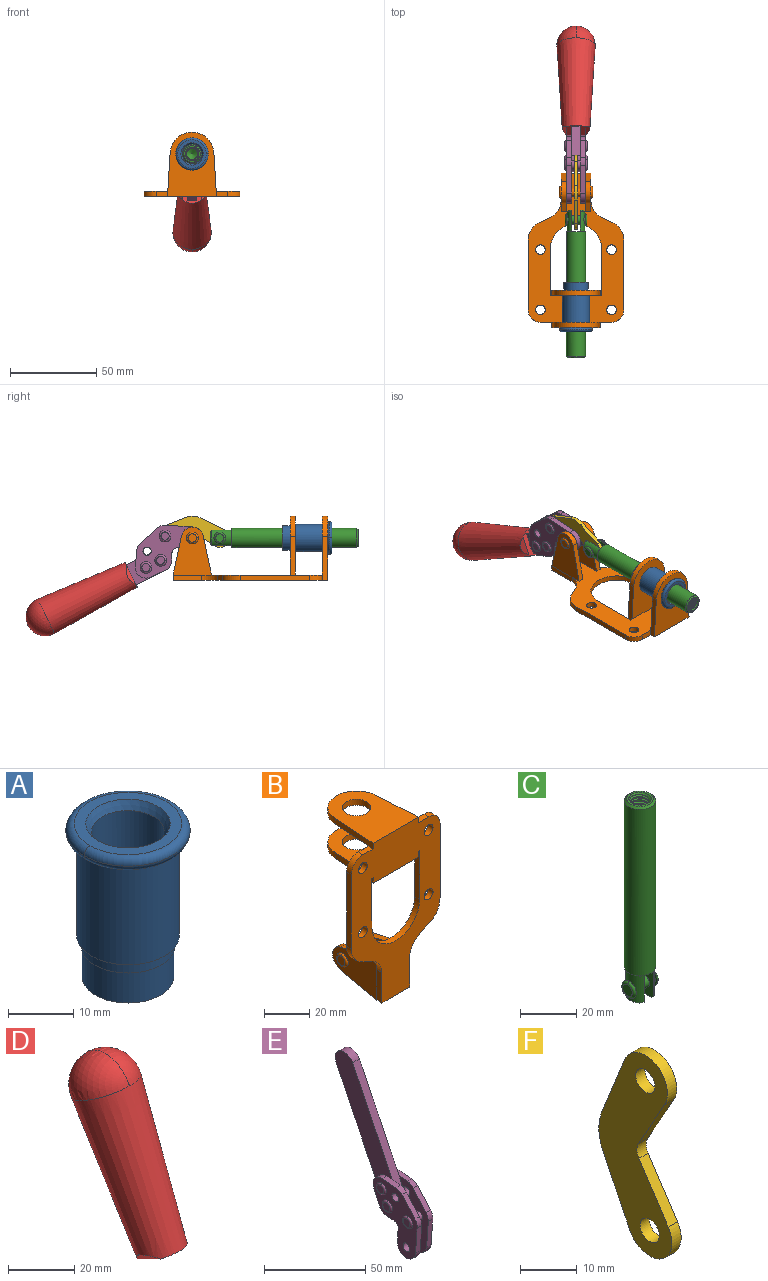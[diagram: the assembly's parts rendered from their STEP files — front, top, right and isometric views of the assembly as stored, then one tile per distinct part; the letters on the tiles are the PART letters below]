
ASSEMBLY  parts=6 mates=6
PART A: 15 faces, bbox 20.6x20.6x28.7 mm
  f0: torus R=8.26mm, axis (0,0,1), area 56.8mm2, adj f1,f10,f12
  f1: torus R=8.26mm, axis (0,0,1), area 56.8mm2, adj f0,f6,f13
  f2: cylinder r=5.59mm len=25.91mm, axis (0,0,1), area 909.6mm2, adj f3,f4
  f3: cone r=6.86mm half-angle=45deg, axis (0,0,-1), area 70.2mm2, adj f2,f14
  f4: cone r=6.47mm half-angle=30deg, axis (0,0,1), area 66.7mm2, adj f2,f13
  f5: cylinder r=7.04mm len=14.07mm, axis (0,0,1), area 252.6mm2, adj f11,f14
  f6: torus R=8.26mm, axis (0,0,1), area 56.8mm2, adj f1,f12,f13
  f7: cylinder r=7.16mm len=14.33mm, axis (0,0,1), area 91.5mm2, adj f9,f11
  f8: cylinder r=7.86mm len=18.42mm, axis (0,0,1), area 909.6mm2, adj f9,f10
  f9: plane 15.72x15.72mm, normal (0,0,-1), area 33mm2, adj f7,f8
  f10: plane 16.51x16.51mm, normal (0,0,-1), area 19.9mm2, adj f0,f8,f12
  f11: plane 14.33x14.33mm, normal (0,0,-1), area 5.7mm2, adj f5,f7
  f12: torus R=8.26mm, axis (0,0,1), area 56.8mm2, adj f0,f6,f10
  f13: plane 16.51x16.51mm, normal (0,0,1), area 82.7mm2, adj f1,f4,f6
  f14: plane 14.07x14.07mm, normal (0,0,-1), area 7.8mm2, adj f3,f5
PART B: 55 faces, bbox 55.7x37.4x89.8 mm
  f0: torus R=2.41mm, axis (-1,0,0), area 15mm2, adj f11,f15,f25
  f1: torus R=2.41mm, axis (-1,0,0), area 15mm2, adj f10,f12,f22
  f2: cylinder r=2.78mm len=5.56mm, axis (0,-1,0), area 54.2mm2, adj f30,f54
  f3: cylinder r=14.99mm len=29.97mm, axis (0,-1,0), area 145.9mm2, adj f30,f49,f53,f54
  f4: cylinder r=2.78mm len=5.56mm, axis (0,-1,0), area 54.2mm2, adj f30,f54
  f5: cylinder r=2.78mm len=5.56mm, axis (0,-1,0), area 54.2mm2, adj f30,f54
  f6: cylinder r=2.78mm len=5.56mm, axis (0,-1,0), area 54.2mm2, adj f30,f54
  f7: cylinder r=6.35mm len=12.7mm, axis (0,0,1), area 123.6mm2, adj f27,f51
  f8: cylinder r=6.35mm len=12.7mm, axis (0,0,-1), area 124.7mm2, adj f21,f35
  f9: cylinder r=2.41mm len=11.18mm, axis (-1,0,0), area 169.4mm2, adj f16,f19
  f10: plane 4.83x4.83mm, normal (1,0,0), area 18.3mm2, adj f1,f12
  f11: plane 4.83x4.83mm, normal (-1,0,0), area 18.3mm2, adj f0,f15
  f12: torus R=2.41mm, axis (-1,0,0), area 15mm2, adj f1,f10,f22
  f13: cylinder r=6.35mm len=12.41mm, axis (1,0,0), area 53.4mm2, adj f18,f19,f22,f23
  f14: cylinder r=6.35mm len=12.41mm, axis (-1,0,0), area 53.4mm2, adj f16,f17,f24,f25
  f15: torus R=2.41mm, axis (-1,0,0), area 15mm2, adj f0,f11,f25
  f16: plane 27.86x22.35mm, normal (1,0,0), area 425.4mm2, adj f9,f14,f17,f24,f30
  f17: plane 22.86x4.97mm, normal (0,0.21,0.98), area 72.5mm2, adj f14,f16,f25,f30
  f18: plane 22.86x4.97mm, normal (0,0.21,0.98), area 72.5mm2, adj f13,f19,f22,f30
  f19: plane 27.86x22.35mm, normal (-1,0,0), area 425.4mm2, adj f9,f13,f18,f23,f30
  f20: cylinder r=12.7mm len=25.35mm, axis (0,0,-1), area 119.8mm2, adj f21,f34,f35,f36
  f21: plane 34.21x28.07mm, normal (0,0,-1), area 702.4mm2, adj f8,f20,f30,f34,f36
  f22: plane 27.96x22.45mm, normal (1,0,0), area 407.2mm2, adj f1,f12,f13,f18,f23,f30,f42,f43
  f23: plane 22.86x4.97mm, normal (0,0.21,-0.98), area 72.5mm2, adj f13,f19,f22,f44
  f24: plane 22.86x4.97mm, normal (0,0.21,-0.98), area 72.5mm2, adj f14,f16,f25,f44
  f25: plane 27.86x22.35mm, normal (-1,0,0), area 407.1mm2, adj f0,f14,f15,f17,f24,f30,f45,f46
  f26: plane 3.1x0.95mm, normal (0,0,-1), area 2.7mm2, adj f30,f49,f50,f54
  f27: plane 34.21x28.07mm, normal (0,0,1), area 702.4mm2, adj f7,f28,f30,f50,f52
  f28: cylinder r=12.7mm len=25.35mm, axis (0,0,1), area 118.8mm2, adj f27,f50,f51,f52
  f29: plane 3.1x0.95mm, normal (0,0,-1), area 2.7mm2, adj f30,f52,f53,f54
  f30: plane 86.54x55.63mm, normal (0,1,0), area 2362.9mm2, adj f2,f3,f4,f5,f6,f16,f17,f18
  f31: plane 40.56x3.1mm, normal (-1,0,0), area 125.7mm2, adj f30,f32,f48,f54
  f32: cylinder r=7.11mm len=7.11mm, axis (0,-1,0), area 34.6mm2, adj f30,f31,f33,f54
  f33: plane 6.67x3.1mm, normal (0,0,1), area 20.4mm2, adj f30,f32,f34,f54
  f34: plane 25.39x3.13mm, normal (-1,0.06,0), area 79.5mm2, adj f20,f21,f33,f35,f54
  f35: plane 37.31x28.45mm, normal (0,0,1), area 789.9mm2, adj f8,f20,f34,f36,f54
  f36: plane 25.39x3.13mm, normal (1,0.06,0), area 79.5mm2, adj f20,f21,f35,f37,f54
  f37: plane 6.67x3.1mm, normal (0,0,1), area 20.4mm2, adj f30,f36,f38,f54
  f38: cylinder r=7.11mm len=7.11mm, axis (0,-1,0), area 34.6mm2, adj f30,f37,f39,f54
  f39: plane 40.56x3.1mm, normal (1,0,0), area 125.7mm2, adj f30,f38,f40,f54
  f40: cylinder r=11.18mm len=10.16mm, axis (0,-1,0), area 39.5mm2, adj f30,f39,f41,f54
  f41: plane 6.09x3.1mm, normal (0.42,0,-0.91), area 20.8mm2, adj f30,f40,f42,f54
  f42: cylinder r=11.18mm len=9.41mm, axis (0,-1,0), area 37.2mm2, adj f22,f30,f41,f43,f54
  f43: plane 16.5x3.1mm, normal (1,0,0), area 51.1mm2, adj f22,f42,f44,f54
  f44: plane 17.37x3.1mm, normal (0,0,-1), area 53.8mm2, adj f23,f24,f30,f43,f45,f54
  f45: plane 16.5x3.1mm, normal (-1,0,0), area 51.1mm2, adj f25,f44,f46,f54
  f46: cylinder r=11.18mm len=9.41mm, axis (0,-1,0), area 37.2mm2, adj f25,f30,f45,f47,f54
  f47: plane 6.09x3.1mm, normal (-0.42,0,-0.91), area 20.8mm2, adj f30,f46,f48,f54
  f48: cylinder r=11.18mm len=10.16mm, axis (0,-1,0), area 39.5mm2, adj f30,f31,f47,f54
  f49: plane 26.54x3.1mm, normal (-1,0,0), area 82.3mm2, adj f3,f26,f30,f54
  f50: plane 25.39x3.1mm, normal (1,0.06,0), area 78.8mm2, adj f26,f27,f28,f51,f54
  f51: plane 37.31x28.45mm, normal (0,0,-1), area 789.9mm2, adj f7,f28,f50,f52,f54
  f52: plane 25.39x3.1mm, normal (-1,0.06,0), area 78.8mm2, adj f27,f28,f29,f51,f54
  f53: plane 26.54x3.1mm, normal (1,0,0), area 82.3mm2, adj f3,f29,f30,f54
  f54: plane 89.66x55.63mm, normal (0,-1,0), area 2678.5mm2, adj f2,f3,f4,f5,f6,f26,f29,f31
PART C: 48 faces, bbox 12.6x11.1x86.1 mm
  f0: torus R=2.41mm, axis (-1,0,0), area 15mm2, adj f30,f32,f34
  f1: torus R=2.41mm, axis (-1,0,0), area 15mm2, adj f29,f31,f33
  f2: cylinder r=5.54mm len=72.39mm, axis (0,0,1), area 2518.5mm2, adj f3,f4,f42,f43
  f3: cone r=5.54mm half-angle=45deg, axis (0,0,1), area 7.6mm2, adj f2,f5,f41
  f4: cone r=5.54mm half-angle=45deg, axis (0,0,-1), area 34.9mm2, adj f2,f39
  f5: cylinder r=5.08mm len=11.48mm, axis (0,0,1), area 108.3mm2, adj f3,f7,f8,f41
  f6: cylinder r=2.41mm len=4.83mm, axis (-1,0,0), area 71.2mm2, adj f40,f41
  f7: cylinder r=2.41mm len=4.83mm, axis (-1,0,0), area 7.6mm2, adj f5,f34
  f8: cone r=5.08mm half-angle=45deg, axis (0,0,1), area 10.6mm2, adj f5,f37,f41
  f9: cone r=3.98mm half-angle=45deg, axis (0,0,1), area 17.6mm2, adj f27,f39,f45,f46,f47
  f10: cylinder r=2.41mm len=4.83mm, axis (-1,0,0), area 7.6mm2, adj f33,f38
  f11: cylinder r=3.2mm len=6.4mm, axis (0,0,1), area 78.4mm2, adj f12,f28,f44,f45,f47
  f12: cylinder r=3.2mm len=6.4mm, axis (0,0,1), area 10.5mm2, adj f11,f13,f45,f47
  f13: cylinder r=3.2mm len=6.4mm, axis (0,0,1), area 10.5mm2, adj f12,f14,f45,f47
  f14: cylinder r=3.2mm len=6.4mm, axis (0,0,1), area 10.5mm2, adj f13,f15,f45,f47
  f15: cylinder r=3.2mm len=6.4mm, axis (0,0,1), area 10.5mm2, adj f14,f16,f45,f47
  f16: cylinder r=3.2mm len=6.4mm, axis (0,0,1), area 10.5mm2, adj f15,f17,f45,f47
  f17: cylinder r=3.2mm len=6.4mm, axis (0,0,1), area 10.5mm2, adj f16,f18,f45,f47
  f18: cylinder r=3.2mm len=6.4mm, axis (0,0,1), area 10.5mm2, adj f17,f19,f45,f47
  f19: cylinder r=3.2mm len=6.4mm, axis (0,0,1), area 10.5mm2, adj f18,f20,f45,f47
  f20: cylinder r=3.2mm len=6.4mm, axis (0,0,1), area 10.5mm2, adj f19,f21,f45,f47
  f21: cylinder r=3.2mm len=6.4mm, axis (0,0,1), area 10.5mm2, adj f20,f22,f45,f47
  f22: cylinder r=3.2mm len=6.4mm, axis (0,0,1), area 10.5mm2, adj f21,f23,f45,f47
  f23: cylinder r=3.2mm len=6.4mm, axis (0,0,1), area 10.5mm2, adj f22,f24,f45,f47
  f24: cylinder r=3.2mm len=6.4mm, axis (0,0,1), area 10.5mm2, adj f23,f25,f45,f47
  f25: cylinder r=3.2mm len=6.4mm, axis (0,0,1), area 10.5mm2, adj f24,f26,f45,f47
  f26: cylinder r=3.2mm len=6.4mm, axis (0,0,1), area 10.5mm2, adj f25,f27,f45,f47
  f27: cylinder r=3.2mm len=6.4mm, axis (0,0,1), area 7.4mm2, adj f9,f26,f45,f47
  f28: cone r=3.2mm half-angle=60deg, axis (0,0,1), area 37.2mm2, adj f11
  f29: plane 4.83x4.83mm, normal (-1,0,0), area 18.3mm2, adj f1,f31
  f30: plane 4.83x4.83mm, normal (1,0,0), area 18.3mm2, adj f0,f32
  f31: torus R=2.41mm, axis (-1,0,0), area 15mm2, adj f1,f29,f33
  f32: torus R=2.41mm, axis (-1,0,0), area 15mm2, adj f0,f30,f34
  f33: plane 6.83x6.83mm, normal (1,0,0), area 18.3mm2, adj f1,f10,f31
  f34: plane 6.83x6.83mm, normal (-1,0,0), area 18.3mm2, adj f0,f7,f32
  f35: cone r=5.08mm half-angle=45deg, axis (0,0,1), area 10.6mm2, adj f36,f38,f40
  f36: plane 7.25x1.97mm, normal (0,0,-1), area 10mm2, adj f35,f40
  f37: plane 7.25x1.97mm, normal (0,0,-1), area 10mm2, adj f8,f41
  f38: cylinder r=5.08mm len=11.48mm, axis (0,0,1), area 108.3mm2, adj f10,f35,f40,f42
  f39: plane 9.55x9.55mm, normal (0,0,1), area 22mm2, adj f4,f9
  f40: plane 12.76x10.09mm, normal (1,0,0), area 95.7mm2, adj f6,f35,f36,f38,f42,f43
  f41: plane 12.76x10.09mm, normal (-1,0,0), area 95.7mm2, adj f3,f5,f6,f8,f37,f43
  f42: cone r=5.54mm half-angle=45deg, axis (0,0,1), area 7.6mm2, adj f2,f38,f40
  f43: plane 11.07x4.7mm, normal (0,0,-1), area 50.4mm2, adj f2,f40,f41
  f44: plane 0.89x0.62mm, normal (-1,0,0), area 0.3mm2, adj f11,f45,f46,f47
  f45: bspline ~24.8x7.63mm, area 266.6mm2, adj f9,f11,f12,f13,f14,f15,f16,f17
  f46: bspline ~24.87x7.63mm, area 73.6mm2, adj f9,f44,f45,f47
  f47: bspline ~24.98x7.63mm, area 272.5mm2, adj f9,f11,f12,f13,f14,f15,f16,f17
PART D: 11 faces, bbox 22.3x42.6x64.5 mm
  f0: sphere r=11.13mm, area 411.4mm2, adj f1,f8
  f1: cone r=11.11mm half-angle=3.3deg, axis (0,0.44,0.9), area 3251.8mm2, adj f0,f7,f8,f9,f10
  f2: cylinder r=6.16mm len=11.7mm, axis (1,0,0), area 89.5mm2, adj f3,f4,f5,f6
  f3: plane 60.23x36.75mm, normal (-1,0,0), area 763.6mm2, adj f2,f4,f6,f10
  f4: plane 51.37x25.05mm, normal (0,0.9,-0.44), area 264.2mm2, adj f2,f3,f5,f10
  f5: plane 60.23x36.75mm, normal (1,0,0), area 763.6mm2, adj f2,f4,f6,f10
  f6: plane 51.37x25.05mm, normal (0,-0.9,0.44), area 264.2mm2, adj f2,f3,f5,f10
  f7: plane 9.95x5.95mm, normal (0.71,-0.31,-0.64), area 25.8mm2, adj f1,f10
  f8: sphere r=11.13mm, area 411.4mm2, adj f0,f1
  f9: plane 9.95x5.95mm, normal (-0.71,-0.31,-0.64), area 25.8mm2, adj f1,f10
  f10: plane 14.27x11.38mm, normal (0,-0.44,-0.9), area 106.7mm2, adj f1,f3,f4,f5,f6,f7,f9
PART E: 59 faces, bbox 12.9x60.2x99.6 mm
  f0: torus R=2.39mm, axis (-1,0,0), area 14.9mm2, adj f20,f43,f51
  f1: torus R=2.39mm, axis (-1,0,0), area 14.9mm2, adj f19,f42,f51
  f2: torus R=2.39mm, axis (-1,0,0), area 14.9mm2, adj f18,f35,f51
  f3: torus R=2.39mm, axis (-1,0,0), area 14.9mm2, adj f14,f17,f23
  f4: torus R=2.39mm, axis (-1,0,0), area 14.9mm2, adj f13,f16,f23
  f5: torus R=2.39mm, axis (-1,0,0), area 14.9mm2, adj f12,f15,f23
  f6: cylinder r=2.39mm len=4.78mm, axis (1,0,0), area 46.5mm2, adj f48,f50,f51
  f7: cylinder r=2.39mm len=4.78mm, axis (1,0,0), area 46.5mm2, adj f50,f51
  f8: cylinder r=6.35mm len=12.68mm, axis (1,0,0), area 61.8mm2, adj f38,f39,f50,f51
  f9: cylinder r=2.39mm len=4.78mm, axis (-1,0,0), area 70.5mm2, adj f46,f50
  f10: cylinder r=2.39mm len=4.78mm, axis (-1,0,0), area 46.5mm2, adj f23,f45,f46
  f11: cylinder r=2.39mm len=4.78mm, axis (-1,0,0), area 46.5mm2, adj f23,f46
  f12: plane 4.78x4.78mm, normal (1,0,0), area 17.9mm2, adj f5,f15
  f13: plane 4.78x4.78mm, normal (1,0,0), area 17.9mm2, adj f4,f16
  f14: plane 4.78x4.78mm, normal (1,0,0), area 17.9mm2, adj f3,f17
  f15: torus R=2.39mm, axis (-1,0,0), area 14.9mm2, adj f5,f12,f23
  f16: torus R=2.39mm, axis (-1,0,0), area 14.9mm2, adj f4,f13,f23
  f17: torus R=2.39mm, axis (-1,0,0), area 14.9mm2, adj f3,f14,f23
  f18: plane 4.78x4.78mm, normal (-1,0,0), area 17.9mm2, adj f2,f35
  f19: plane 4.78x4.78mm, normal (-1,0,0), area 17.9mm2, adj f1,f42
  f20: plane 4.78x4.78mm, normal (-1,0,0), area 17.9mm2, adj f0,f43
  f21: plane 2.26x0.2mm, normal (1,0,0), area 0.2mm2, adj f31,f44
  f22: plane 2.26x0.2mm, normal (-1,0,0), area 0.2mm2, adj f41,f44
  f23: plane 39.37x30.77mm, normal (1,0,0), area 565.5mm2, adj f3,f4,f5,f10,f11,f15,f16,f17
  f24: cylinder r=6.1mm len=4.15mm, axis (-1,0,0), area 14.7mm2, adj f23,f25,f32,f46
  f25: plane 10.25x9.01mm, normal (0,-0.75,0.66), area 42.3mm2, adj f23,f24,f26,f46
  f26: cylinder r=6.35mm len=4.64mm, axis (-1,0,0), area 15.6mm2, adj f23,f25,f27,f46
  f27: plane 15.84x3.1mm, normal (0,-1,-0.07), area 49.2mm2, adj f23,f26,f28,f46
  f28: cylinder r=6.35mm len=12.68mm, axis (-1,0,0), area 61.8mm2, adj f23,f27,f29,f46
  f29: plane 8.11x3.1mm, normal (0,1,0.07), area 25.2mm2, adj f23,f28,f30,f46
  f30: cylinder r=3.05mm len=3.25mm, axis (-1,0,0), area 14.8mm2, adj f23,f29,f31,f46
  f31: plane 5.99x3.1mm, normal (0,0.07,-1), area 18.6mm2, adj f21,f23,f30,f44,f46
  f32: plane 9.5x3.1mm, normal (0,-0.07,1), area 29.5mm2, adj f23,f24,f33,f46,f47
  f33: cylinder r=6.1mm len=8.63mm, axis (-1,0,0), area 39.1mm2, adj f23,f32,f34,f47
  f34: plane 8.65x3.96mm, normal (0,0.91,-0.42), area 29.5mm2, adj f23,f33,f44,f47
  f35: torus R=2.39mm, axis (-1,0,0), area 14.9mm2, adj f2,f18,f51
  f36: plane 10.25x9.01mm, normal (0,-0.75,0.66), area 42.3mm2, adj f37,f49,f50,f51
  f37: cylinder r=6.35mm len=4.64mm, axis (1,0,0), area 15.6mm2, adj f36,f38,f50,f51
  f38: plane 15.84x3.1mm, normal (0,-1,-0.07), area 49.2mm2, adj f8,f37,f50,f51
  f39: plane 8.11x3.1mm, normal (0,1,0.07), area 25.2mm2, adj f8,f40,f50,f51
  f40: cylinder r=3.05mm len=3.25mm, axis (1,0,0), area 14.8mm2, adj f39,f41,f50,f51
  f41: plane 5.99x3.1mm, normal (0,0.07,-1), area 18.6mm2, adj f22,f40,f44,f50,f51
  f42: torus R=2.39mm, axis (-1,0,0), area 14.9mm2, adj f1,f19,f51
  f43: torus R=2.39mm, axis (-1,0,0), area 14.9mm2, adj f0,f20,f51
  f44: cylinder r=6.35mm len=12.12mm, axis (-1,0,0), area 128.9mm2, adj f21,f22,f23,f31,f34,f41,f46,f47
  f45: plane 2.65x1.35mm, normal (1,0,0), area 1mm2, adj f10,f55
  f46: plane 39.08x20.42mm, normal (-1,0,0), area 412.5mm2, adj f9,f10,f11,f24,f25,f26,f27,f28
  f47: plane 77.62x39.82mm, normal (1,0,0), area 850mm2, adj f32,f33,f34,f44,f53,f54,f55
  f48: plane 2.65x1.35mm, normal (-1,0,0), area 1mm2, adj f6,f55
  f49: cylinder r=6.1mm len=4.15mm, axis (1,0,0), area 14.7mm2, adj f36,f50,f51,f56
  f50: plane 39.08x20.42mm, normal (1,0,0), area 412.5mm2, adj f6,f7,f8,f9,f36,f37,f38,f39
  f51: plane 39.37x30.77mm, normal (-1,0,0), area 565.5mm2, adj f0,f1,f2,f6,f7,f8,f35,f36
  f52: plane 8.65x3.96mm, normal (0,0.91,-0.42), area 29.5mm2, adj f44,f51,f57,f58
  f53: plane 68.49x33.4mm, normal (0,0.9,-0.44), area 358.1mm2, adj f44,f47,f54,f58
  f54: cylinder r=6.35mm len=12.06mm, axis (1,0,0), area 93.7mm2, adj f47,f53,f55,f58
  f55: plane 68.49x33.4mm, normal (0,-0.9,0.44), area 358.1mm2, adj f44,f45,f46,f47,f48,f50,f54,f58
  f56: plane 9.5x3.1mm, normal (0,-0.07,1), area 29.5mm2, adj f49,f50,f51,f57,f58
  f57: cylinder r=6.1mm len=8.63mm, axis (1,0,0), area 39.1mm2, adj f51,f52,f56,f58
  f58: plane 77.62x39.82mm, normal (-1,0,0), area 850mm2, adj f44,f52,f53,f54,f55,f56,f57
PART F: 12 faces, bbox 2.3x18.2x42.8 mm
  f0: cylinder r=2.4mm len=4.8mm, axis (1,0,0), area 34.9mm2, adj f4,f11
  f1: cylinder r=10.41mm len=8.47mm, axis (1,0,0), area 20.2mm2, adj f4,f9,f10,f11
  f2: cylinder r=3.05mm len=3.16mm, axis (1,0,0), area 7.7mm2, adj f4,f6,f7,f11
  f3: cylinder r=2.4mm len=4.8mm, axis (1,0,0), area 34.9mm2, adj f4,f11
  f4: plane 42.81x18.23mm, normal (-1,0,0), area 414.1mm2, adj f0,f1,f2,f3,f5,f6,f7,f8
  f5: cylinder r=5.54mm len=10.67mm, axis (1,0,0), area 41.8mm2, adj f4,f6,f10,f11
  f6: plane 11.66x6.53mm, normal (0,-0.87,-0.49), area 30.9mm2, adj f2,f4,f5,f11
  f7: plane 11.17x7.33mm, normal (0,-0.84,0.55), area 30.9mm2, adj f2,f4,f8,f11
  f8: cylinder r=5.54mm len=10.51mm, axis (1,0,0), area 41.8mm2, adj f4,f7,f9,f11
  f9: plane 13.67x6.67mm, normal (0,0.9,-0.44), area 35.1mm2, adj f1,f4,f8,f11
  f10: plane 14.1x5.7mm, normal (0,0.93,0.37), area 35.1mm2, adj f1,f4,f5,f11
  f11: plane 42.81x18.23mm, normal (1,0,0), area 414.1mm2, adj f0,f1,f2,f3,f5,f6,f7,f8
PLACE A rot(axis=(1,0,0),90deg) t=(0,9.14,0)mm
PLACE B rot(axis=(1,0,0),90deg) t=(0,9.14,0)mm fixed
PLACE C rot(axis=(1,0,0),90deg) t=(0,40.81,0)mm
PLACE D rot(axis=(-1,0,0),90deg) t=(0.04,73.33,49.23)mm
PLACE E rot(axis=(-1,0,0),90deg) t=(0,73.33,49.23)mm
PLACE F rot(axis=(1,0,0),94deg) t=(0,42.49,1.14)mm
MATE slider C.f2 <-> B.f7  axis (0,-1,0) through (0,-17.97,24.61)mm
MATE revolute F.f3 <-> E.f4  axis (1,0,0) through (0,57.07,25.72)mm
MATE revolute F.f5 <-> C.f6  axis (1,0,0) through (0,25.34,24.61)mm
MATE revolute E.f7 <-> B.f0  axis (-1,0,0) through (0,41.23,24.61)mm
MATE fastened D.f2 <-> E.f54  axis (-1,0,0) through (2.35,128.1,-21.81)mm
MATE fastened A.f0 <-> B.f7  axis (0,1,0) through (0,-37.25,24.61)mm
